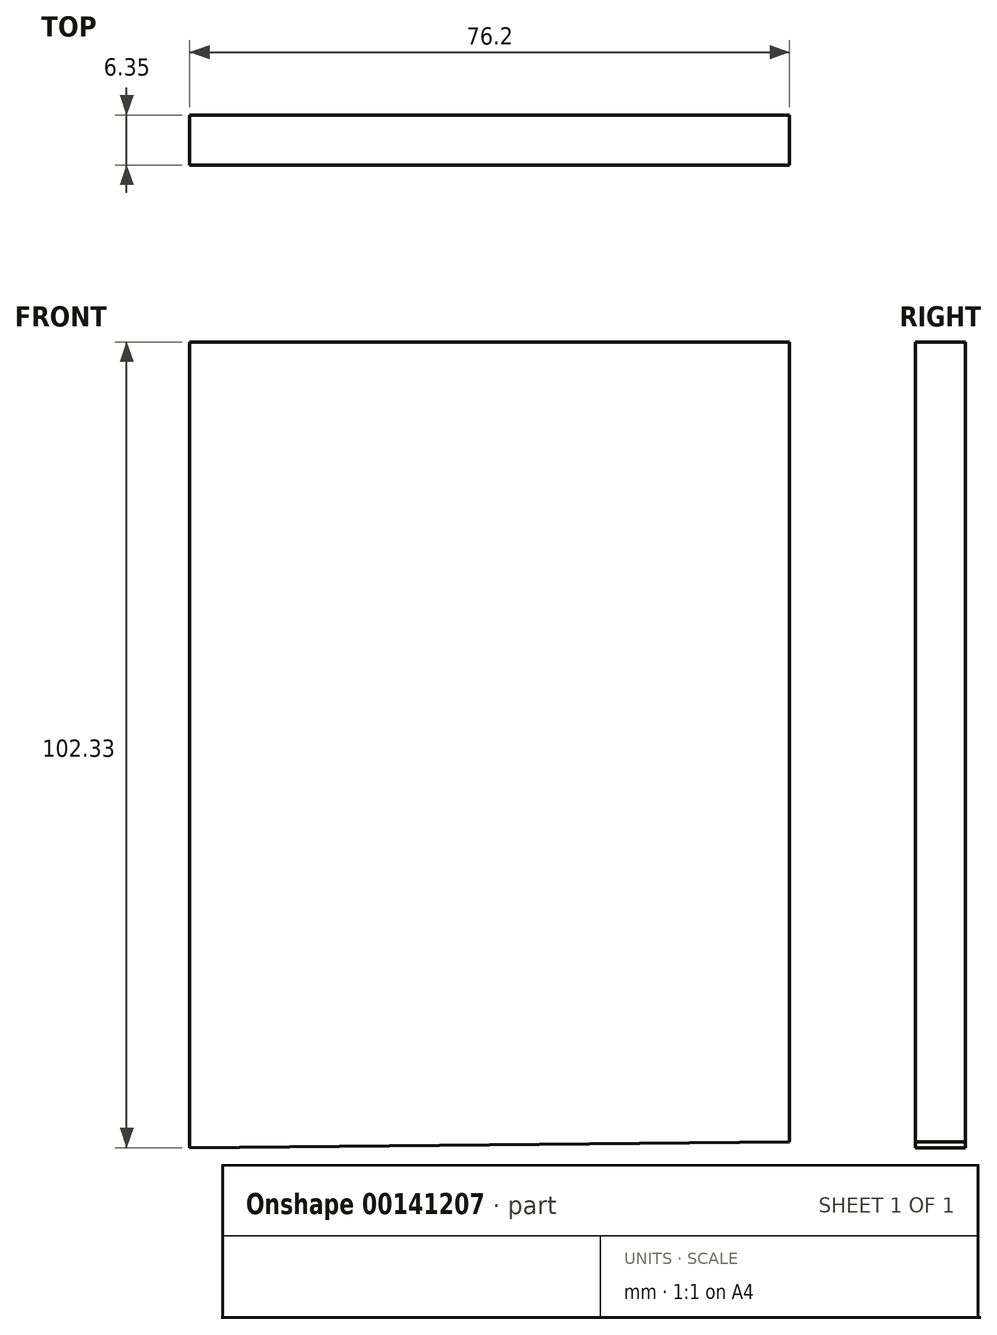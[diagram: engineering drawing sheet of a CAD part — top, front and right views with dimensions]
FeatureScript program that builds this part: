
annotation { "Feature Type Name" : "Feature", "Feature Type Description" : "" }
export const myFeature = defineFeature(function(context is Context, id is Id, definition is map)
    precondition{}
    {
        {
            var Q0;
            Q0=qCreatedBy(makeId("Front.planeOp"),FACE);
            var sketch = newSketch(context, id + "F0", { "sketchPlane" : qUnion([Q0])});
            skLineSegment(sketch, "E0", {"start": v(0, 0) * mm, "end": v(69.27, 0) * mm});
            skLineSegment(sketch, "E1", {"start": v(76.2, 0.73) * mm, "end": v(76.2, 102.33) * mm});
            skLineSegment(sketch, "E2", {"start": v(0, 0) * mm, "end": v(76.2, 0.73) * mm});
            skLineSegment(sketch, "E3", {"start": v(0, 0) * mm, "end": v(0, 102.33) * mm});
            skLineSegment(sketch, "E4", {"start": v(0, 102.33) * mm, "end": v(76.2, 102.33) * mm});
            skSolve(sketch);
        }
        {
            var Q0;
            Q0 = qSketchRegion(id + "F0", true);
            extrude(context, id + "F1", {"entities" : qUnion([Q0]), "depth" : 6.35 * mm});
        }
    });
